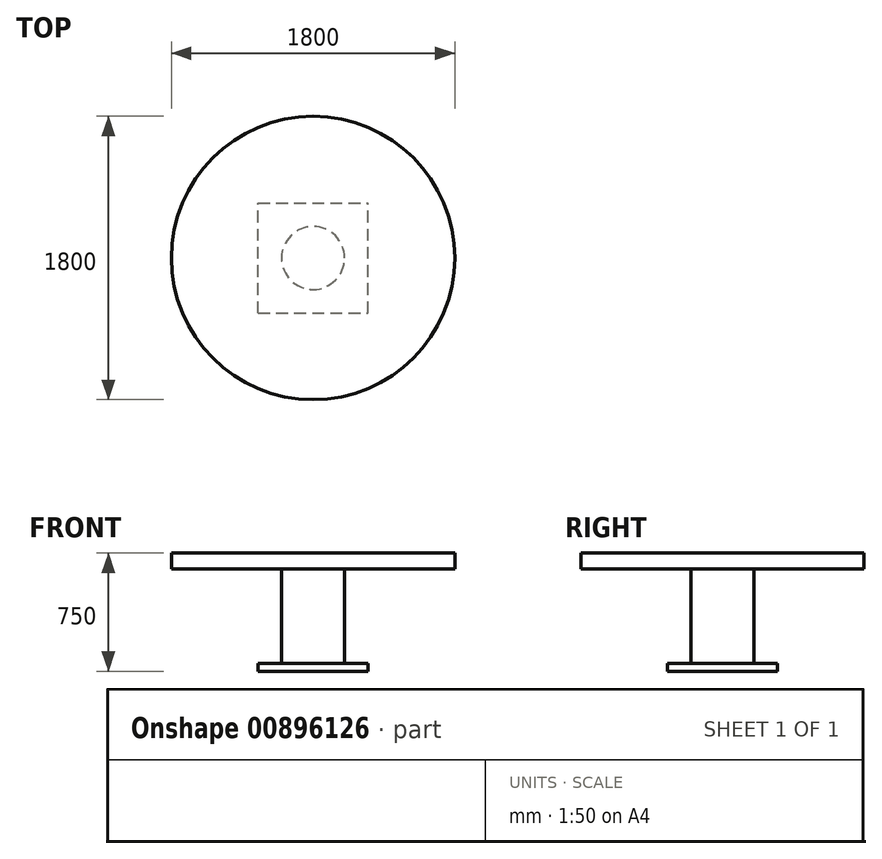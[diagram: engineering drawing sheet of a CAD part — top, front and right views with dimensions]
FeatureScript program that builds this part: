
annotation { "Feature Type Name" : "Feature", "Feature Type Description" : "" }
export const myFeature = defineFeature(function(context is Context, id is Id, definition is map)
    precondition{}
    {
        {
            var Q0;
            Q0=qCreatedBy(makeId("Top.planeOp"),FACE);
            var sketch = newSketch(context, id + "F0", { "sketchPlane" : qUnion([Q0])});
            skCircle(sketch, "E0", {"center": v(0, 0) * mm, "radius": 900 * mm});
            skCircle(sketch, "E1", {"center": v(0, 0) * mm, "radius": 200 * mm});
            skLineSegment(sketch, "E2.bottom", {"start": v(-350, -350) * mm, "end": v(350, -350) * mm});
            skLineSegment(sketch, "E2.top", {"start": v(-350, 350) * mm, "end": v(350, 350) * mm});
            skLineSegment(sketch, "E2.left", {"start": v(-350, -350) * mm, "end": v(-350, 350) * mm});
            skLineSegment(sketch, "E2.right", {"start": v(350, -350) * mm, "end": v(350, 350) * mm});
            skLineSegment(sketch, "E3", {"start": v(-350, 0) * mm, "end": v(350, 0) * mm, "construction": true});
            skLineSegment(sketch, "E4", {"start": v(0, -350) * mm, "end": v(0, 350) * mm, "construction": true});
            skSolve(sketch);
        }
        {
            var Q0;
            Q0=makeQuery(id+"F0.imprint","IMPRINT",FACE,{"disambiguationData":[TD([[makeQuery(id+"F0.imprint","IMPRINT",EDGE,{"derivedFrom":sQuery(id+"F0.wireOp",EDGE,"E0")}),1.0]])]});
            var Q1;
            Q1=makeQuery(id+"F0.imprint","IMPRINT",FACE,{"disambiguationData":[TD([[makeQuery(id+"F0.imprint","IMPRINT",EDGE,{"derivedFrom":sQuery(id+"F0.wireOp",EDGE,"E1")}),-1.0]])]});
            var Q2;
            Q2=makeQuery(id+"F0.imprint","IMPRINT",FACE,{"disambiguationData":[TD([[makeQuery(id+"F0.imprint","IMPRINT",EDGE,{"derivedFrom":sQuery(id+"F0.wireOp",EDGE,"E1")}),1.0]])]});
            extrude(context, id + "F1", {"entities" : qUnion([Q0, Q1, Q2]), "depth" : 100 * mm, "offsetDistance" : 25 * mm});
        }
        {
            var Q0;
            Q0=makeQuery(id+"F0.imprint","IMPRINT",FACE,{"disambiguationData":[TD([[makeQuery(id+"F0.imprint","IMPRINT",EDGE,{"derivedFrom":sQuery(id+"F0.wireOp",EDGE,"E1")}),1.0]])]});
            extrude(context, id + "F2", {"entities" : qUnion([Q0]), "operationType" : NewBodyOperationType.ADD, "depth" : -600 * mm, "offsetDistance" : 25 * mm});
        }
        {
            var Q0;
            Q0=makeQuery(id+"F0.imprint","IMPRINT",FACE,{"disambiguationData":[TD([[makeQuery(id+"F0.imprint","IMPRINT",EDGE,{"derivedFrom":sQuery(id+"F0.wireOp",EDGE,"E1")}),-1.0]])]});
            var Q1;
            Q1=makeQuery(id+"F0.imprint","IMPRINT",FACE,{"disambiguationData":[TD([[makeQuery(id+"F0.imprint","IMPRINT",EDGE,{"derivedFrom":sQuery(id+"F0.wireOp",EDGE,"E1")}),1.0]])]});
            extrude(context, id + "F3", {"entities" : qUnion([Q0, Q1]), "operationType" : NewBodyOperationType.ADD, "oppositeDirection" : true, "depth" : 650 * mm, "offsetDistance" : 25 * mm, "hasSecondDirection" : true, "secondDirectionOppositeDirection" : true, "secondDirectionDepth" : 600 * mm});
        }
    });
